# Revit family: Fin_wall
name_source: partatom
category: Generic Models
revit_build: Autodesk Revit 2018 (Build: 20170223_1515(x64)
units: mm (PartAtom-declared; Revit-internal decimal feet)

## family parameters
Always vertical = Yes
Can host rebar = No
Cut with Voids When Loaded = No
Part Type = Normal
Room Calculation Point = No
Round Connector Dimension = Use Diameter
Shared = No
Work Plane-Based = No

## types (1)
- Fin_wall
    Depth to foundation = 750 mm
    Steel thickness = 10 mm  [stored 0.0328084 ft]
    Steel width = 150 mm
    Timber max. tolerance = 4 mm  [stored 0.0131234 ft]
    Timber min. tolerance = 2 mm  [stored 0.00656168 ft]
    Timber thickness = 38 mm  [stored 0.124672 ft]
    Timber width = 200 mm  [stored 0.656168 ft]
    Top constraint = 1800 mm  [stored 5.90551 ft]

note: [stored X ft] marks values corroborated as IEEE doubles in the binary element streams (Revit-internal decimal feet)

## geometry (parser evidence)
native form markers: Sweep x1
no freeform markers — native parametric forms only
